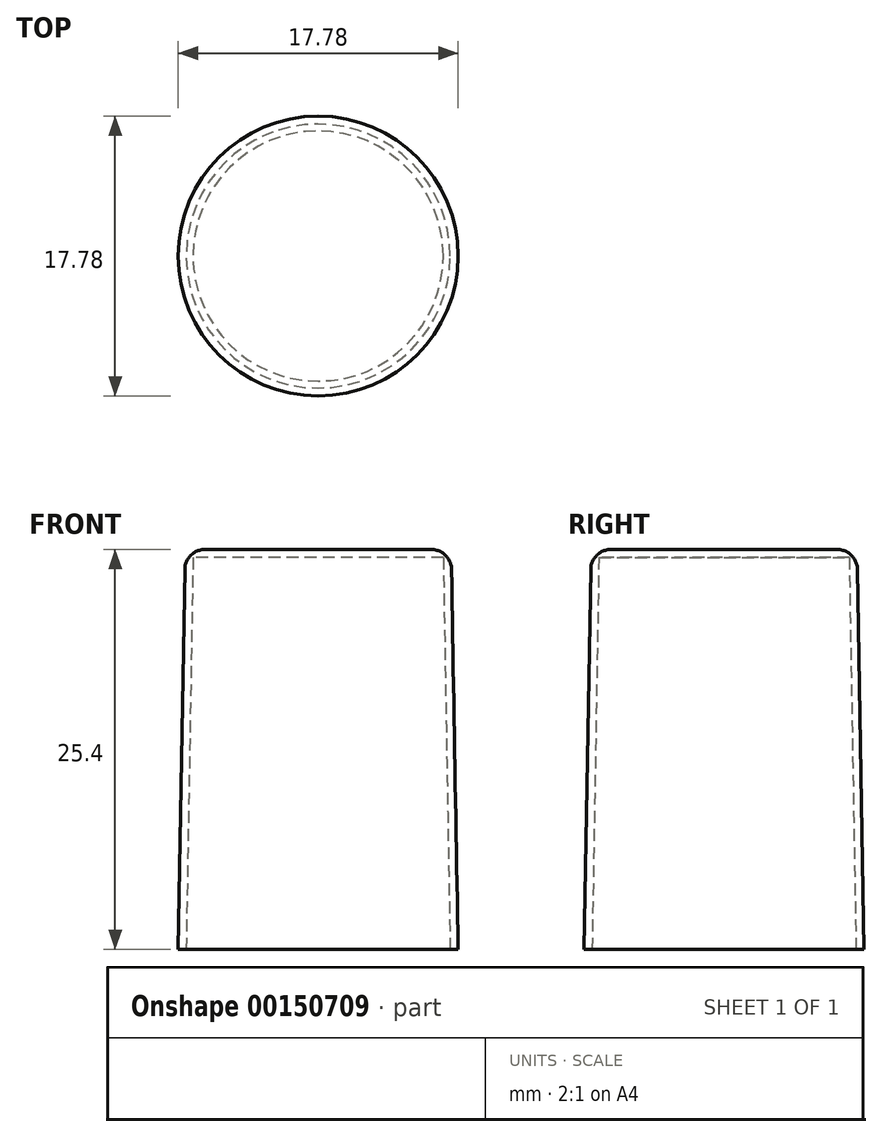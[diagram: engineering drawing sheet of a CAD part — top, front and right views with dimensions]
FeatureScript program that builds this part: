
annotation { "Feature Type Name" : "Feature", "Feature Type Description" : "" }
export const myFeature = defineFeature(function(context is Context, id is Id, definition is map)
    precondition{}
    {
        {
            var Q0;
            Q0=qCreatedBy(makeId("Top.planeOp"),FACE);
            var sketch = newSketch(context, id + "F0", { "sketchPlane" : qUnion([Q0])});
            skCircle(sketch, "E0", {"center": v(0, 0) * mm, "radius": 8.9 * mm});
            skSolve(sketch);
        }
        {
            var Q0;
            Q0 = qSketchRegion(id + "F0", true);
            extrude(context, id + "F1", {"entities" : qUnion([Q0]), "depth" : 25.4 * mm, "hasDraft" : true, "draftAngle" : 1 * degree, "draftPullDirection" : true});
        }
        {
            var Q0;
            Q0=makeQuery(id+"F1.opExtrude","CAP_FACE",FACE,{"disambiguationData":[OSD([sQuery(id+"F0.wireOp",EDGE,"E0")])],"isStart":true});
            shell(context, id + "F2", {"entities" : qUnion([Q0]), "thickness" : 0.5 * mm});
        }
        {
            var Q0;
            Q0=makeQuery(id+"F1.opExtrude","CAP_FACE",FACE,{"disambiguationData":[OSD([sQuery(id+"F0.wireOp",EDGE,"E0")])],"isStart":false});
            fillet(context, id + "F3", {"entities" : qUnion([Q0]), "radius" : 1.27 * mm, "tangentPropagation" : true, "allowEdgeOverflow" : false});
        }
    });
